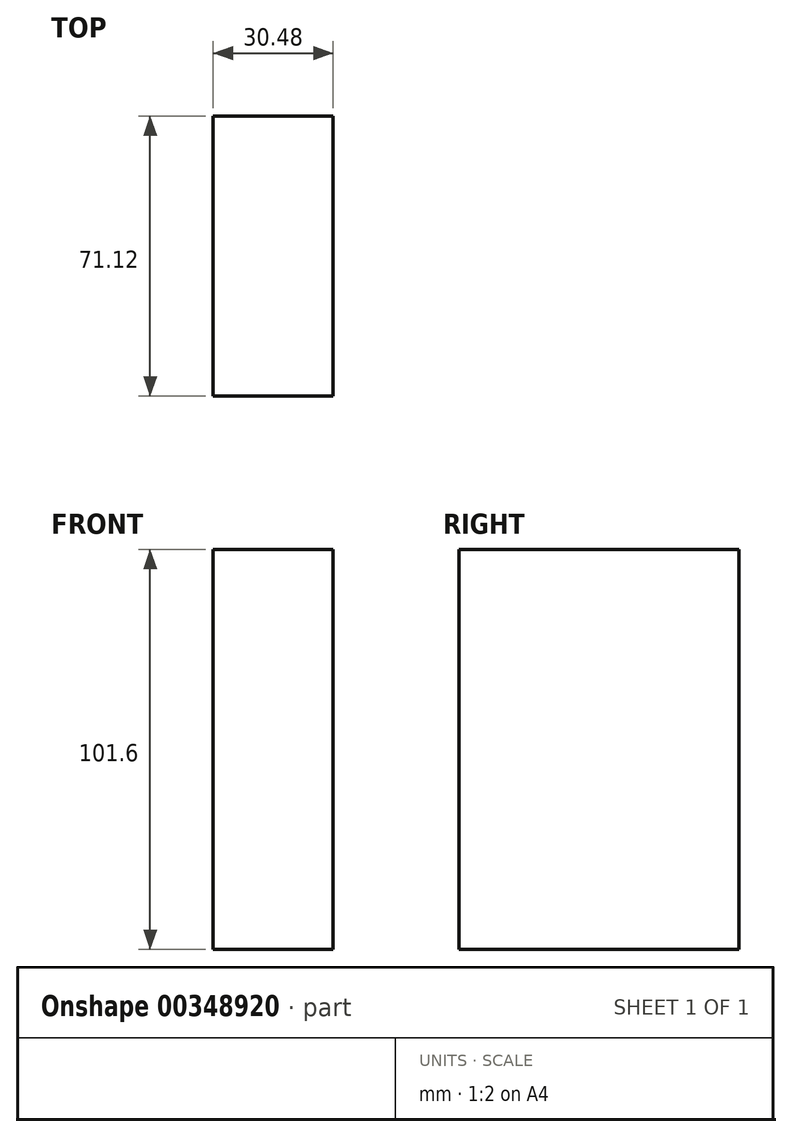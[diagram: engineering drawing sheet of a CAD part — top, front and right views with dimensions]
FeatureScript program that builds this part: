
annotation { "Feature Type Name" : "Feature", "Feature Type Description" : "" }
export const myFeature = defineFeature(function(context is Context, id is Id, definition is map)
    precondition{}
    {
        {
            var Q0;
            Q0=qCreatedBy(makeId("Top.planeOp"),FACE);
            var sketch = newSketch(context, id + "F0", { "sketchPlane" : qUnion([Q0])});
            skLineSegment(sketch, "E0.bottom", {"start": v(0, 0) * mm, "end": v(30.48, 0) * mm});
            skLineSegment(sketch, "E0.top", {"start": v(0, 71.12) * mm, "end": v(30.48, 71.12) * mm});
            skLineSegment(sketch, "E0.left", {"start": v(0, 0) * mm, "end": v(0, 71.12) * mm});
            skLineSegment(sketch, "E0.right", {"start": v(30.48, 0) * mm, "end": v(30.48, 71.12) * mm});
            skSolve(sketch);
        }
        {
            var Q0;
            Q0 = qSketchRegion(id + "F0", true);
            extrude(context, id + "F1", {"entities" : qUnion([Q0]), "depth" : 101.6 * mm});
        }
    });
